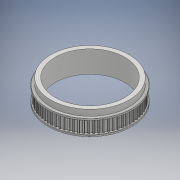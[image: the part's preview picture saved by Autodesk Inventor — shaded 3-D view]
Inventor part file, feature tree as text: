
AUTODESK INVENTOR PART (.ipt)
format: ipt  version: 2018 (Build 220112000, 112)  size: 715,776 bytes
history: native  units: mm
features: extrude x6, sketch x5, other x1, pattern_circular x1, fillet x1
ambient origin geometry x8: Origin, YZ Plane, XZ Plane, XY Plane, X Axis, Y Axis, Z Axis, Center Point
bodies: Solid1 (feature_tree)
feature tree (14):
  other  "Tooth"
  extrude  "Gear Solid Extrusion"  Depth=1.5mm
  extrude  "Tooth Cut-Out Extrusion"  Depth=0.85mm
  pattern_circular  "Teeth Array"  [2 undecoded]
  extrude  "Flange Extrusion Front"  Depth=10.0mm TaperAngle=0.0deg
  extrude  "Flange Extrusion Back"  Depth=5.0mm
  fillet  "Flange Fillet"  [1 undecoded]
  extrude  "Boss Extrusion"  Depth=34.422538mm
  extrude  "Bore Extrusion"  TaperAngle=0.0deg  [1 undecoded]
  sketch  "Sketch2"  dims[d2=33.422538mm d3=1.5mm]
  sketch  "Sketch3"  dims[d4=1.14mm d5=0.85mm]
  sketch  "Sketch4"  dims[d6=0.61mm]
  sketch  "Sketch5"  dims[d7=0.25mm]
  sketch  "Sketch6"  dims[d8=2.0mm d11=0.0mm d12=10.0mm d13=0.0mm d14=700.0mm d15=360.0deg d17=34.422538mm d19=0.0mm d20=34.422538mm d21=1.5mm d22=0.0mm d23=0.25mm d26=32.1mm d27=5.0mm d28=0.0mm d29=28.6mm d30=5.0mm d31=0.0mm]
note: 4 required parameter values undecoded (feature->parameter linkage not recoverable at this tier; creation-order binding heuristic only, values carry confidence <= 0.55)
